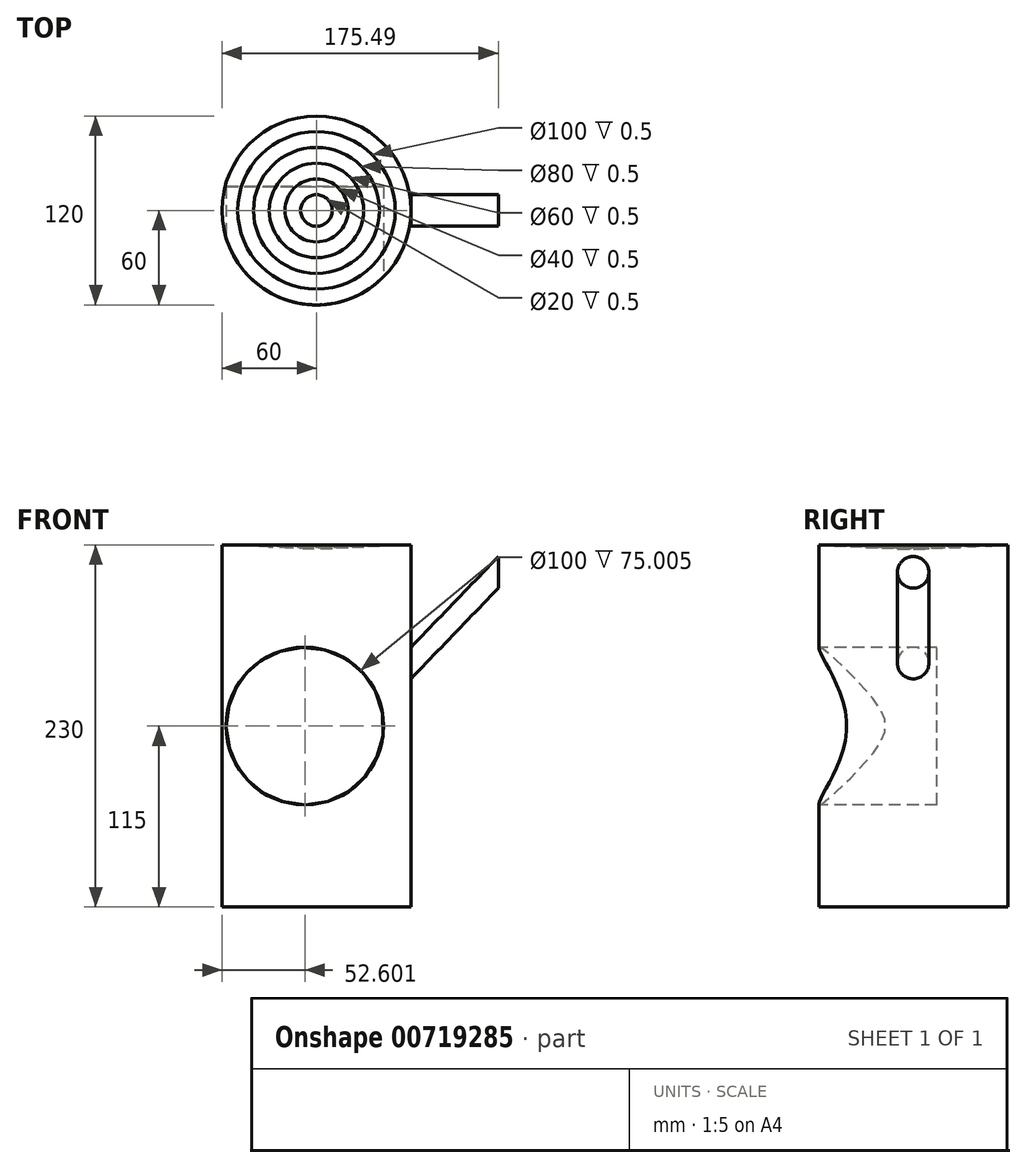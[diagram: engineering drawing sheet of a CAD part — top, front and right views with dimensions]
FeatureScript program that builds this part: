
annotation { "Feature Type Name" : "Feature", "Feature Type Description" : "" }
export const myFeature = defineFeature(function(context is Context, id is Id, definition is map)
    precondition{}
    {
        {
            var Q0;
            Q0=qCreatedBy(makeId("Front.planeOp"),FACE);
            cPlane(context, id + "F0", {"entities" : qUnion([Q0]), "cplaneType" : CPlaneType.OFFSET, "offset" : 60 * mm, "width" : 150 * mm, "height" : 150 * mm});
        }
        {
            var Q0;
            Q0=qCreatedBy(makeId("Front.planeOp"),FACE);
            var sketch = newSketch(context, id + "F1", { "sketchPlane" : qUnion([Q0])});
            skLineSegment(sketch, "E0", {"start": v(0, 0) * mm, "end": v(0, 115) * mm});
            skLineSegment(sketch, "E1", {"start": v(0, 115) * mm, "end": v(60, 115) * mm});
            skLineSegment(sketch, "E2", {"start": v(60, 115) * mm, "end": v(60, -115) * mm});
            skLineSegment(sketch, "E3", {"start": v(60, -115) * mm, "end": v(0, -115) * mm});
            skLineSegment(sketch, "E4", {"start": v(0, -115) * mm, "end": v(0, 0) * mm});
            skSolve(sketch);
        }
        {
            var Q0;
            Q0=makeQuery(id+"F1.imprint","IMPRINT",FACE,{"disambiguationData":[TD([[makeQuery(id+"F1.imprint","IMPRINT",EDGE,{"derivedFrom":sQuery(id+"F1.wireOp",EDGE,"E0")}),-1.0]])]});
            var Q1;
            Q1=sQuery(id+"F1.wireOp",EDGE,"E0");
            revolve(context, id + "F2", {"surfaceOperationType" : NewSurfaceOperationType.NEW, "entities" : qUnion([Q0]), "axis" : qUnion([Q1]), "revolveType" : RevolveType.FULL});
        }
        {
            var Q0;
            Q0=qCreatedBy(id+"F0.planeOp",FACE);
            var sketch = newSketch(context, id + "F3", { "sketchPlane" : qUnion([Q0])});
            skCircle(sketch, "E5", {"center": v(-7.4, 0) * mm, "radius": 50 * mm});
            skSolve(sketch);
        }
        {
            var Q0;
            Q0=makeQuery(id+"F3.imprint","IMPRINT",FACE,{"disambiguationData":[TD([[makeQuery(id+"F3.imprint","IMPRINT",EDGE,{"derivedFrom":sQuery(id+"F3.wireOp",EDGE,"E5")}),1.0]])]});
            extrude(context, id + "F4", {"entities" : qUnion([Q0]), "operationType" : NewBodyOperationType.REMOVE, "oppositeDirection" : true, "depth" : 75 * mm, "offsetDistance" : 25 * mm});
        }
        {
            var Q0;
            Q0=makeQuery(id+"F2.opRevolve","SWEPT_FACE",FACE,{"disambiguationData":[OSD([sQuery(id+"F1.wireOp",EDGE,"E1")])]});
            var sketch = newSketch(context, id + "F5", { "sketchPlane" : qUnion([Q0])});
            skCircle(sketch, "E6", {"center": v(0, 0) * mm, "radius": 50 * mm});
            skSolve(sketch);
        }
        {
            var Q0;
            Q0=makeQuery(id+"F5.imprint","IMPRINT",FACE,{"disambiguationData":[TD([[makeQuery(id+"F5.imprint","IMPRINT",EDGE,{"derivedFrom":sQuery(id+"F5.wireOp",EDGE,"E6")}),1.0]])]});
            extrude(context, id + "F6", {"entities" : qUnion([Q0]), "operationType" : NewBodyOperationType.REMOVE, "oppositeDirection" : true, "depth" : 0.5 * mm, "offsetDistance" : 25 * mm});
        }
        {
            var Q0;
            Q0=makeQuery(id+"F6.boolean.opBoolean","COPY",FACE,{"derivedFrom":makeQuery(id+"F6.opExtrude","CAP_FACE",FACE,{"disambiguationData":[OSD([sQuery(id+"F5.wireOp",EDGE,"E6")])],"isStart":false})});
            var sketch = newSketch(context, id + "F7", { "sketchPlane" : qUnion([Q0])});
            skCircle(sketch, "E7", {"center": v(0, 0) * mm, "radius": 40 * mm});
            skSolve(sketch);
        }
        {
            var Q0;
            Q0=makeQuery(id+"F7.imprint","IMPRINT",FACE,{"disambiguationData":[TD([[makeQuery(id+"F7.imprint","IMPRINT",EDGE,{"derivedFrom":sQuery(id+"F7.wireOp",EDGE,"E7")}),1.0]])]});
            extrude(context, id + "F8", {"entities" : qUnion([Q0]), "operationType" : NewBodyOperationType.REMOVE, "oppositeDirection" : true, "depth" : .5 * mm, "offsetDistance" : 25 * mm});
        }
        {
            var Q0;
            Q0=makeQuery(id+"F8.boolean.opBoolean","COPY",FACE,{"derivedFrom":makeQuery(id+"F8.opExtrude","CAP_FACE",FACE,{"disambiguationData":[OSD([sQuery(id+"F7.wireOp",EDGE,"E7")])],"isStart":false})});
            var sketch = newSketch(context, id + "F9", { "sketchPlane" : qUnion([Q0])});
            skCircle(sketch, "E8", {"center": v(0, 0) * mm, "radius": 30 * mm});
            skSolve(sketch);
        }
        {
            var Q0;
            Q0=makeQuery(id+"F9.imprint","IMPRINT",FACE,{"disambiguationData":[TD([[makeQuery(id+"F9.imprint","IMPRINT",EDGE,{"derivedFrom":sQuery(id+"F9.wireOp",EDGE,"E8")}),1.0]])]});
            extrude(context, id + "F10", {"entities" : qUnion([Q0]), "operationType" : NewBodyOperationType.REMOVE, "oppositeDirection" : true, "depth" : 0.5 * mm, "offsetDistance" : 25 * mm});
        }
        {
            var Q0;
            Q0=makeQuery(id+"F10.boolean.opBoolean","COPY",FACE,{"derivedFrom":makeQuery(id+"F10.opExtrude","CAP_FACE",FACE,{"disambiguationData":[OSD([sQuery(id+"F9.wireOp",EDGE,"E8")])],"isStart":false})});
            var sketch = newSketch(context, id + "F11", { "sketchPlane" : qUnion([Q0])});
            skCircle(sketch, "E9", {"center": v(0, 0) * mm, "radius": 20 * mm});
            skSolve(sketch);
        }
        {
            var Q0;
            Q0 = qSketchRegion(id + "F11", true);
            extrude(context, id + "F12", {"entities" : qUnion([Q0]), "operationType" : NewBodyOperationType.REMOVE, "oppositeDirection" : true, "depth" : 0.5 * mm, "offsetDistance" : 25 * mm});
        }
        {
            var Q0;
            Q0=makeQuery(id+"F12.boolean.opBoolean","COPY",FACE,{"derivedFrom":makeQuery(id+"F12.opExtrude","CAP_FACE",FACE,{"disambiguationData":[OSD([sQuery(id+"F11.wireOp",EDGE,"E9")])],"isStart":false})});
            var sketch = newSketch(context, id + "F13", { "sketchPlane" : qUnion([Q0])});
            skCircle(sketch, "E10", {"center": v(0, 0) * mm, "radius": 10 * mm});
            skSolve(sketch);
        }
        {
            var Q0;
            Q0 = qSketchRegion(id + "F13", true);
            extrude(context, id + "F14", {"entities" : qUnion([Q0]), "operationType" : NewBodyOperationType.REMOVE, "oppositeDirection" : true, "depth" : 0.5 * mm, "offsetDistance" : 25 * mm});
        }
        {
            var Q0;
            Q0=qCreatedBy(makeId("Right.planeOp"),FACE);
            cPlane(context, id + "F15", {"entities" : qUnion([Q0]), "cplaneType" : CPlaneType.OFFSET, "offset" : 60 * mm, "width" : 150 * mm, "height" : 150 * mm});
        }
        {
            var Q0;
            Q0=qCreatedBy(id+"F15.planeOp",FACE);
            var sketch = newSketch(context, id + "F16", { "sketchPlane" : qUnion([Q0])});
            skCircle(sketch, "E11", {"center": v(0, 40) * mm, "radius": 10 * mm});
            skSolve(sketch);
        }
        {
            var Q0;
            Q0=qCreatedBy(makeId("Front.planeOp"),FACE);
            var sketch = newSketch(context, id + "F17", { "sketchPlane" : qUnion([Q0])});
            skLineSegment(sketch, "E12", {"start": v(60.51, 39.84) * mm, "end": v(116, 97.47) * mm});
            skSolve(sketch);
        }
        {
            var Q0;
            Q0=makeQuery(id+"F16.imprint","IMPRINT",FACE,{"disambiguationData":[TD([[makeQuery(id+"F16.imprint","IMPRINT",EDGE,{"derivedFrom":sQuery(id+"F16.wireOp",EDGE,"E11")}),1.0]])]});
            var Q1;
            Q1=sQuery(id+"F17.wireOp",EDGE,"E12");
            sweep(context, id + "F18", {"operationType" : NewBodyOperationType.ADD, "profiles" : qUnion([Q0]), "path" : qUnion([Q1])});
        }
    });
